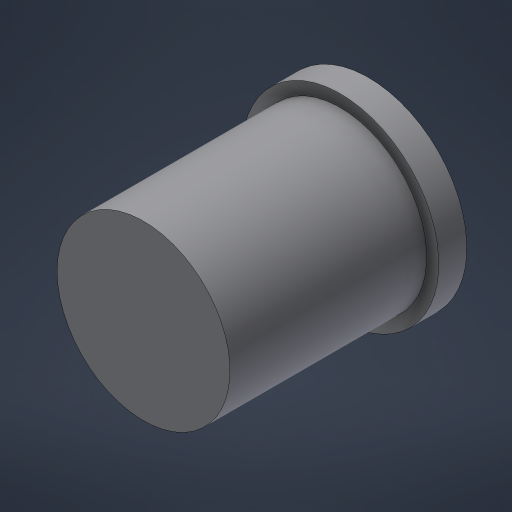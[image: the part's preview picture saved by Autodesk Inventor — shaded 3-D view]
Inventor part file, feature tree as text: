
AUTODESK INVENTOR PART (.ipt)
format: ipt  version: 2023.5 (Build 275446000, 446)  size: 181,760 bytes
history: native  units: mm
features: revolve x1, sketch x1
ambient origin geometry x8: Origin, YZ Plane, XZ Plane, XY Plane, X Axis, Y Axis, Z Axis, Center Point
bodies: Volumenkörper1 (feature_tree)
feature tree (2):
  revolve  "Umdrehung1"
  sketch  "Skizze1"  dims[d0=12.3mm d1=14.0mm d2=14.0mm d3=2.0mm d4=90.0deg]
